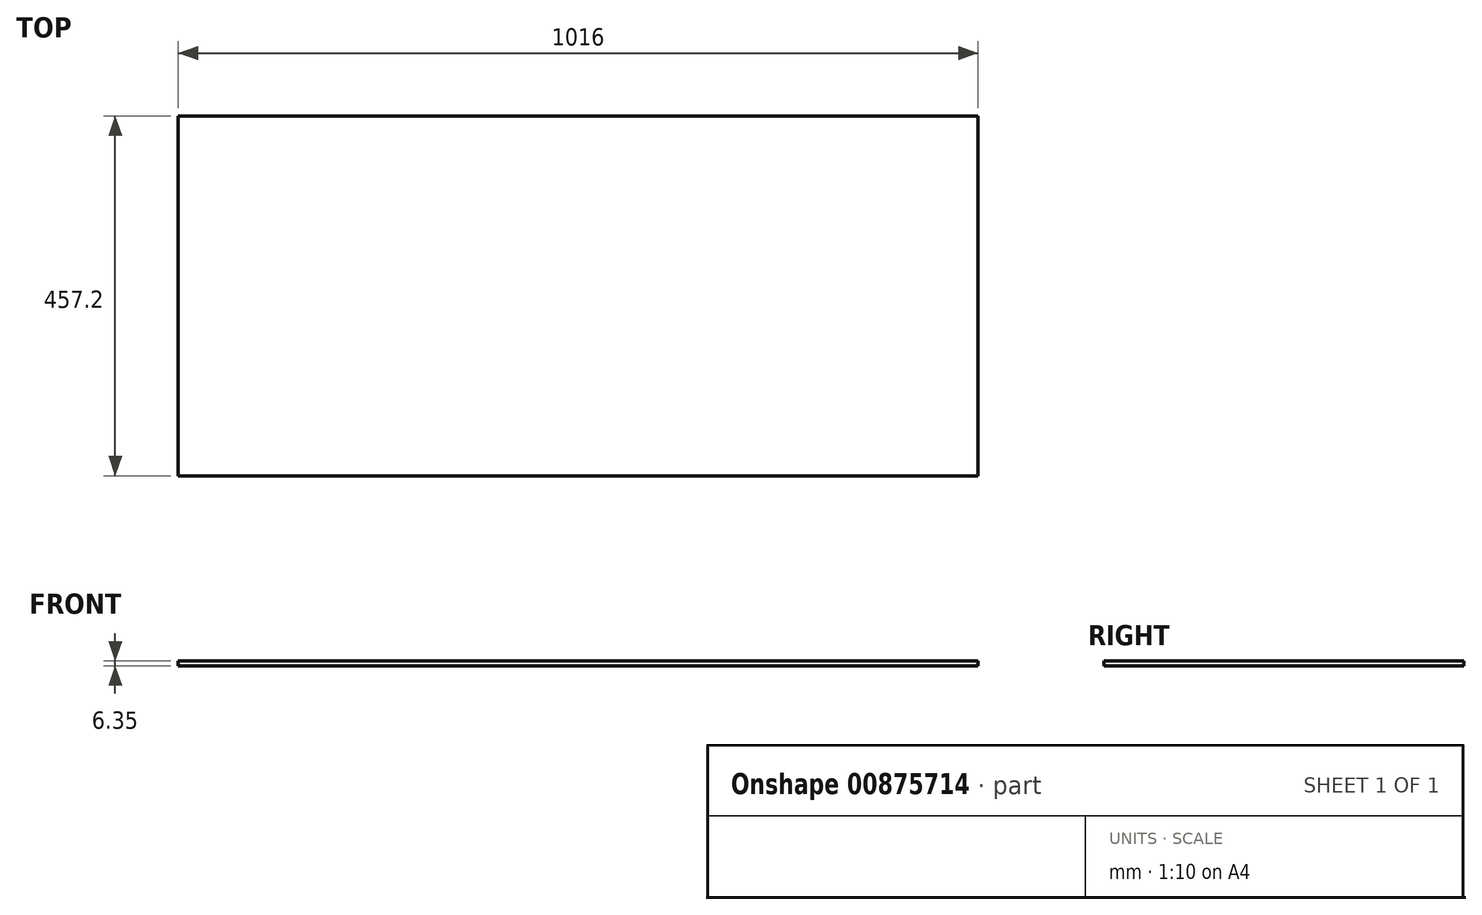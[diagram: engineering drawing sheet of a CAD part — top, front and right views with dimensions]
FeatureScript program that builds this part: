
annotation { "Feature Type Name" : "Feature", "Feature Type Description" : "" }
export const myFeature = defineFeature(function(context is Context, id is Id, definition is map)
    precondition{}
    {
        {
            var Q0;
            Q0=qCreatedBy(makeId("Top.planeOp"),FACE);
            var sketch = newSketch(context, id + "F0", { "sketchPlane" : qUnion([Q0])});
            skLineSegment(sketch, "E0.bottom", {"start": v(508, -228.6) * mm, "end": v(-508, -228.6) * mm});
            skLineSegment(sketch, "E0.top", {"start": v(508, 228.6) * mm, "end": v(-508, 228.6) * mm});
            skLineSegment(sketch, "E0.left", {"start": v(508, -228.6) * mm, "end": v(508, 228.6) * mm});
            skLineSegment(sketch, "E0.right", {"start": v(-508, -228.6) * mm, "end": v(-508, 228.6) * mm});
            skPoint(sketch, "E0.middle", {"position": v(0, 0) * mm});
            skSolve(sketch);
        }
        {
            var Q0;
            Q0 = qSketchRegion(id + "F0", true);
            extrude(context, id + "F1", {"entities" : qUnion([Q0]), "depth" : 6.35 * mm, "offsetDistance" : 25.4 * mm});
        }
    });
